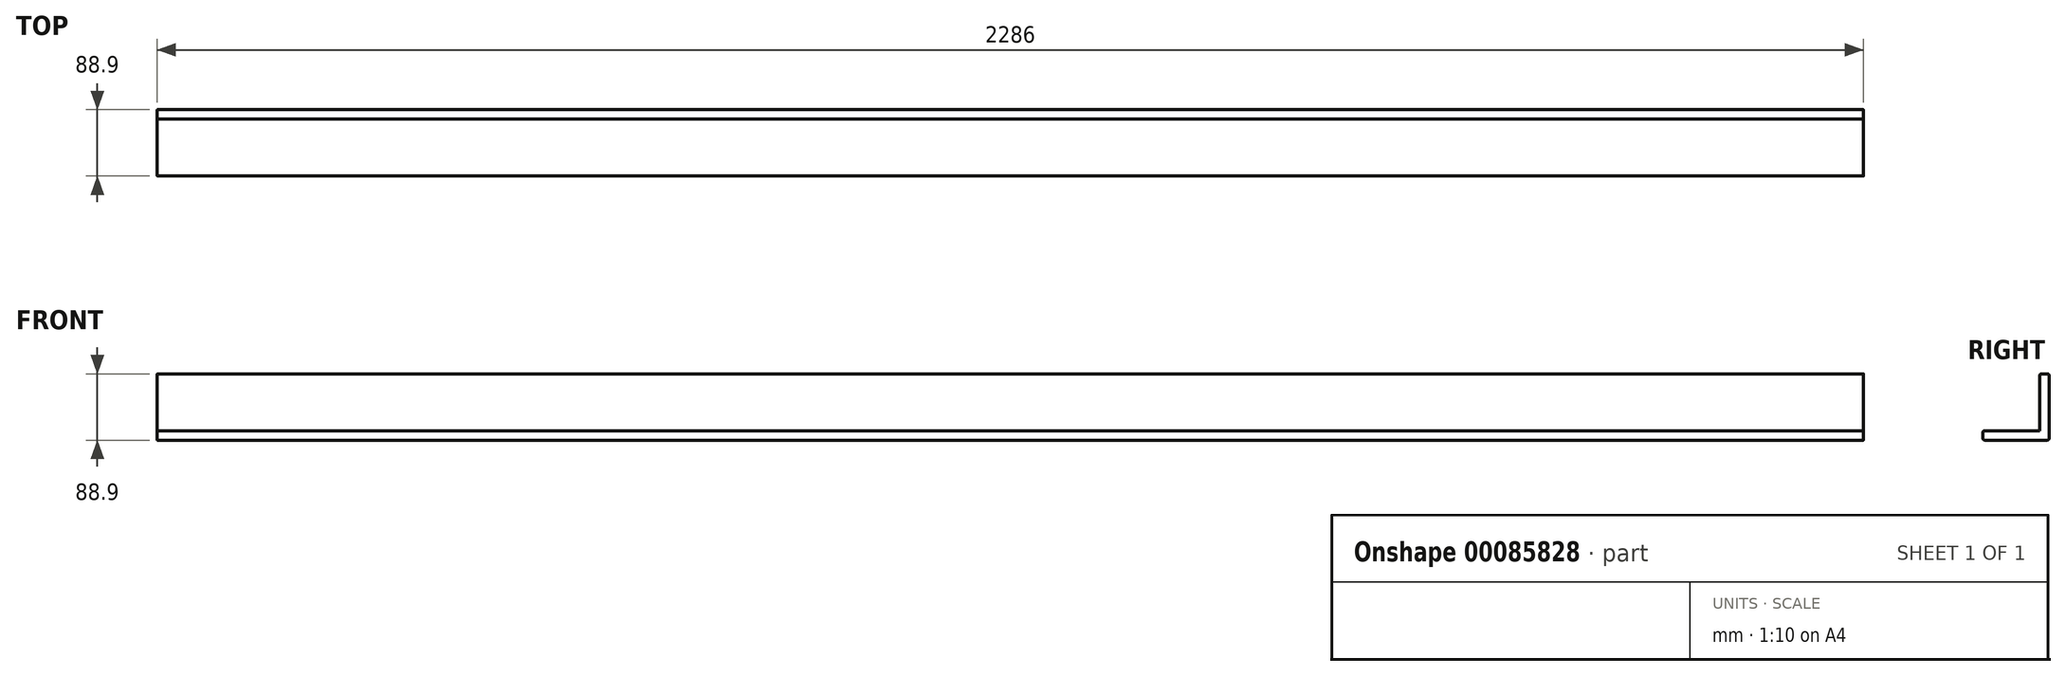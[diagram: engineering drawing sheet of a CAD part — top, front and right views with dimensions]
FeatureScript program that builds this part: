
annotation { "Feature Type Name" : "Feature", "Feature Type Description" : "" }
export const myFeature = defineFeature(function(context is Context, id is Id, definition is map)
    precondition{}
    {
        {
            var Q0;
            Q0=qCreatedBy(makeId("Right.planeOp"),FACE);
            var sketch = newSketch(context, id + "F0", { "sketchPlane" : qUnion([Q0])});
            skLineSegment(sketch, "E0", {"start": v(-9.4, 64.73) * mm, "end": v(-9.4, -11.47) * mm});
            skLineSegment(sketch, "E1", {"start": v(-9.4, -11.47) * mm, "end": v(-85.6, -11.47) * mm});
            skLineSegment(sketch, "E2", {"start": v(3.3, 64.73) * mm, "end": v(3.3, -24.17) * mm});
            skLineSegment(sketch, "E3", {"start": v(-85.6, -24.17) * mm, "end": v(3.3, -24.17) * mm});
            skLineSegment(sketch, "E4", {"start": v(-9.4, 64.73) * mm, "end": v(3.3, 64.73) * mm});
            skLineSegment(sketch, "E5", {"start": v(-85.6, -24.17) * mm, "end": v(-85.6, -11.47) * mm});
            skSolve(sketch);
        }
        {
            var Q0;
            Q0=makeQuery(id+"F0.imprint","IMPRINT",FACE,{"disambiguationData":[TD([[makeQuery(id+"F0.imprint","IMPRINT",EDGE,{"derivedFrom":sQuery(id+"F0.wireOp",EDGE,"E0")}),1.0]])]});
            extrude(context, id + "F1", {"entities" : qUnion([Q0]), "depth" : 2286 * mm, "offsetDistance" : 25.4 * mm});
        }
        {
            var Q0;
            Q0=makeQuery(id+"F1.opExtrude","SWEPT_EDGE",EDGE,{"disambiguationData":[OSD([sQuery(id+"F0.wireOp",EDGE,"E2"),sQuery(id+"F0.wireOp",EDGE,"E4")])]});
            var Q1;
            Q1=makeQuery(id+"F1.opExtrude","SWEPT_EDGE",EDGE,{"disambiguationData":[OSD([sQuery(id+"F0.wireOp",EDGE,"E0"),sQuery(id+"F0.wireOp",EDGE,"E4")])]});
            var Q2;
            Q2=makeQuery(id+"F1.opExtrude","SWEPT_EDGE",EDGE,{"disambiguationData":[OSD([sQuery(id+"F0.wireOp",EDGE,"E2"),sQuery(id+"F0.wireOp",EDGE,"E3")])]});
            var Q3;
            Q3=makeQuery(id+"F1.opExtrude","SWEPT_EDGE",EDGE,{"disambiguationData":[OSD([sQuery(id+"F0.wireOp",EDGE,"E1"),sQuery(id+"F0.wireOp",EDGE,"E5")])]});
            var Q4;
            Q4=makeQuery(id+"F1.opExtrude","SWEPT_EDGE",EDGE,{"disambiguationData":[OSD([sQuery(id+"F0.wireOp",EDGE,"E3"),sQuery(id+"F0.wireOp",EDGE,"E5")])]});
            fillet(context, id + "F2", {"entities" : qUnion([Q0, Q1, Q2, Q3, Q4]), "radius" : 2.54 * mm, "tangentPropagation" : true, "allowEdgeOverflow" : false});
        }
    });
